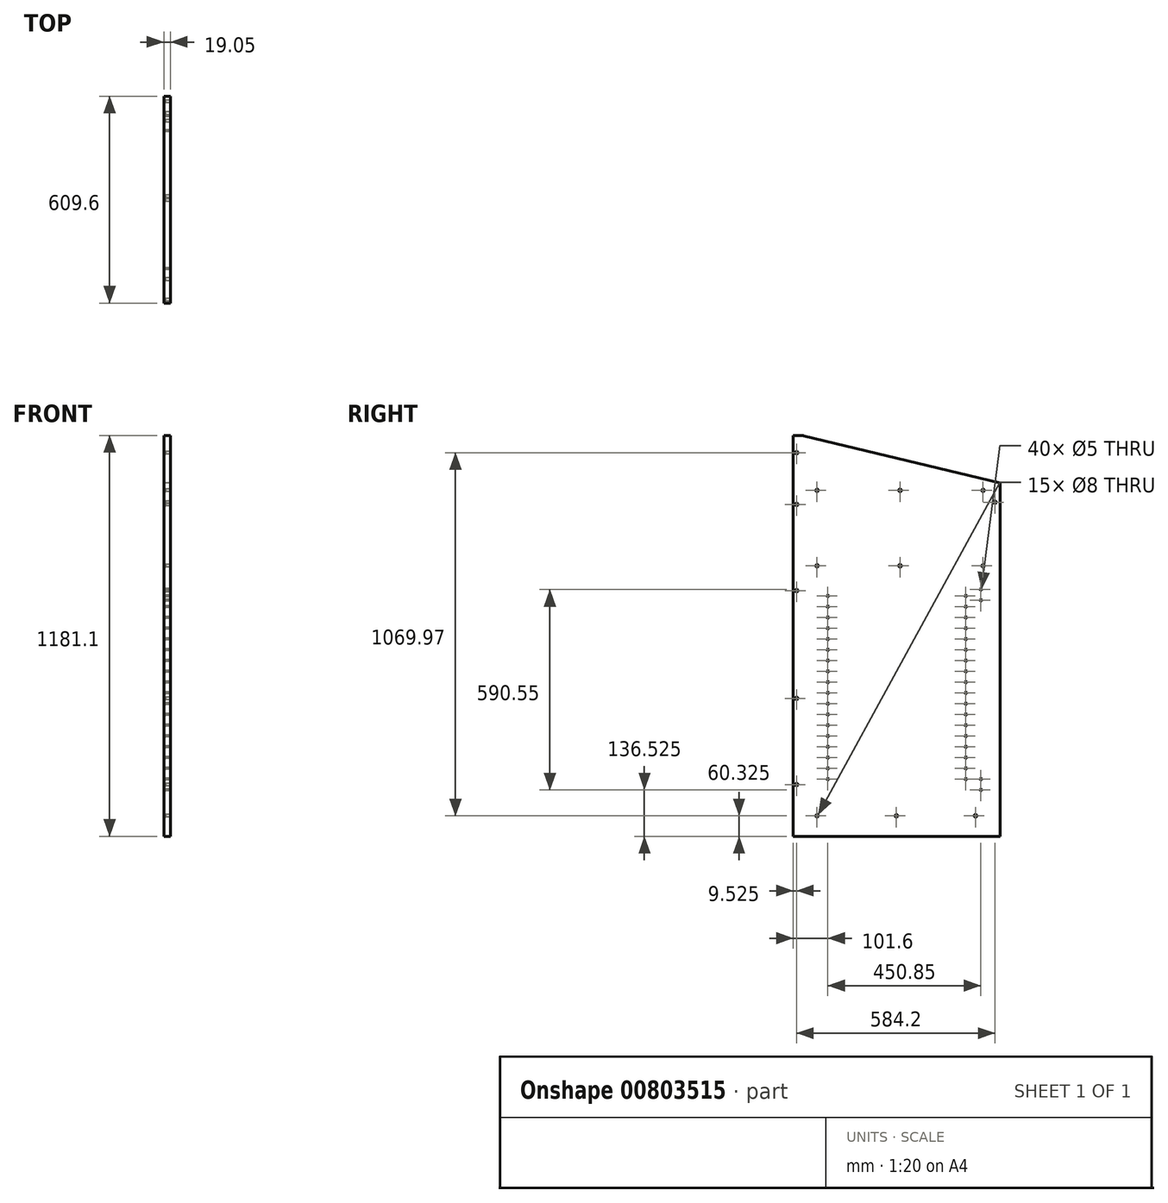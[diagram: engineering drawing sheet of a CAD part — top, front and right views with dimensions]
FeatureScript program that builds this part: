
annotation { "Feature Type Name" : "Feature", "Feature Type Description" : "" }
export const myFeature = defineFeature(function(context is Context, id is Id, definition is map)
    precondition{}
    {
        {
            var Q0;
            Q0=qCreatedBy(makeId("Right.planeOp"),FACE);
            var sketch = newSketch(context, id + "F0", { "sketchPlane" : qUnion([Q0])});
            skLineSegment(sketch, "E0.bottom", {"start": v(304.8, 590.55) * mm, "end": v(-304.8, 590.55) * mm});
            skLineSegment(sketch, "E0.top", {"start": v(304.8, -590.55) * mm, "end": v(-304.8, -590.55) * mm});
            skLineSegment(sketch, "E0.left", {"start": v(304.8, 590.55) * mm, "end": v(304.8, -590.55) * mm});
            skLineSegment(sketch, "E0.right", {"start": v(-304.8, 590.55) * mm, "end": v(-304.8, -590.55) * mm});
            skPoint(sketch, "E0.middle", {"position": v(0, 0) * mm});
            skLineSegment(sketch, "E1", {"start": v(304.8, 590.55) * mm, "end": v(285.39, 590.55) * mm});
            skLineSegment(sketch, "E2", {"start": v(-304.8, 590.55) * mm, "end": v(-304.8, 450.85) * mm});
            skLineSegment(sketch, "E3", {"start": v(-304.8, 450.85) * mm, "end": v(273.57, 589.16) * mm});
            skPoint(sketch, "E4.visualSharp", {"position": v(279.4, 590.55) * mm});
            skArc(sketch, "E4.filletArc", {"start": v(285.39, 590.55) * mm, "mid": v(279.44, 590.2) * mm, "end": v(273.57, 589.16) * mm});
            skLineSegment(sketch, "E5", {"start": v(-304.8, 450.85) * mm, "end": v(-304.8, 428.62) * mm});
            skSolve(sketch);
        }
        {
            var Q0;
            Q0=makeQuery(id+"F0.imprint","IMPRINT",FACE,{"disambiguationData":[TD([[makeQuery(id+"F0.imprint","IMPRINT",EDGE,{"derivedFrom":sQuery(id+"F0.wireOp",EDGE,"E0.top")}),-1.0]])]});
            extrude(context, id + "F1", {"entities" : qUnion([Q0]), "depth" : 19.05 * mm, "offsetDistance" : 25.4 * mm});
        }
        {
            var Q0;
            Q0=makeQuery(id+"F1.opExtrude","CAP_FACE",FACE,{"disambiguationData":[OSD([sQuery(id+"F0.wireOp",EDGE,"E0.top"),sQuery(id+"F0.wireOp",EDGE,"E0.left"),sQuery(id+"F0.wireOp",EDGE,"E0.right"),sQuery(id+"F0.wireOp",EDGE,"E1"),sQuery(id+"F0.wireOp",EDGE,"E3"),sQuery(id+"F0.wireOp",EDGE,"E4.filletArc"),sQuery(id+"F0.wireOp",EDGE,"E5")])],"isStart":false});
            var sketch = newSketch(context, id + "F2", { "sketchPlane" : qUnion([Q0])});
            skLineSegment(sketch, "E6.bottom", {"start": v(304.8, 590.55) * mm, "end": v(285.75, 590.55) * mm});
            skLineSegment(sketch, "E6.top", {"start": v(304.8, -590.55) * mm, "end": v(285.75, -590.55) * mm});
            skLineSegment(sketch, "E6.left", {"start": v(304.8, 590.55) * mm, "end": v(304.8, -590.55) * mm});
            skLineSegment(sketch, "E6.right", {"start": v(285.75, 590.55) * mm, "end": v(285.75, -590.55) * mm});
            skLineSegment(sketch, "E7", {"start": v(295.1, 590.55) * mm, "end": v(295.1, 539.75) * mm});
            skLineSegment(sketch, "E8", {"start": v(295.1, 590.55) * mm, "end": v(295.1, 387.35) * mm});
            skLineSegment(sketch, "E9", {"start": v(295.1, 590.55) * mm, "end": v(295.1, 133.35) * mm});
            skLineSegment(sketch, "E10", {"start": v(295.28, -590.55) * mm, "end": v(295.28, -438.15) * mm});
            skLineSegment(sketch, "E11", {"start": v(295.28, -590.55) * mm, "end": v(295.28, -184.15) * mm});
            skPoint(sketch, "E12", {"position": v(295.1, 539.75) * mm});
            skPoint(sketch, "E13", {"position": v(295.1, 387.35) * mm});
            skPoint(sketch, "E14", {"position": v(295.1, 133.35) * mm});
            skPoint(sketch, "E15", {"position": v(295.28, -184.15) * mm});
            skPoint(sketch, "E16", {"position": v(295.28, -438.15) * mm});
            skLineSegment(sketch, "E17", {"start": v(-304.8, 450.85) * mm, "end": v(-304.8, 438.15) * mm});
            skLineSegment(sketch, "E18.bottom", {"start": v(-304.8, 438.15) * mm, "end": v(285.75, 438.15) * mm});
            skLineSegment(sketch, "E18.top", {"start": v(-304.8, 419.1) * mm, "end": v(285.75, 419.1) * mm});
            skLineSegment(sketch, "E18.left", {"start": v(-304.8, 438.15) * mm, "end": v(-304.8, 419.1) * mm});
            skLineSegment(sketch, "E18.right", {"start": v(285.75, 438.15) * mm, "end": v(285.75, 419.1) * mm});
            skLineSegment(sketch, "E19", {"start": v(-304.8, -590.55) * mm, "end": v(-304.8, -539.75) * mm});
            skLineSegment(sketch, "E20", {"start": v(-304.8, -539.75) * mm, "end": v(-282.57, -539.75) * mm});
            skLineSegment(sketch, "E21.bottom", {"start": v(-282.57, -539.75) * mm, "end": v(285.75, -539.75) * mm});
            skLineSegment(sketch, "E21.top", {"start": v(-282.57, -511.18) * mm, "end": v(285.75, -511.18) * mm});
            skLineSegment(sketch, "E21.left", {"start": v(-282.57, -539.75) * mm, "end": v(-282.57, -511.18) * mm});
            skLineSegment(sketch, "E21.right", {"start": v(285.75, -539.75) * mm, "end": v(285.75, -511.18) * mm});
            skLineSegment(sketch, "E22", {"start": v(-304.8, 428.62) * mm, "end": v(-254, 428.62) * mm});
            skLineSegment(sketch, "E23", {"start": v(-9.52, 438.15) * mm, "end": v(-9.52, 428.62) * mm});
            skLineSegment(sketch, "E24", {"start": v(285.75, 428.62) * mm, "end": v(234.95, 428.62) * mm});
            skLineSegment(sketch, "E25", {"start": v(-304.8, 419.1) * mm, "end": v(-298.45, 419.1) * mm});
            skLineSegment(sketch, "E26.bottom", {"start": v(-298.45, 419.1) * mm, "end": v(-279.4, 419.1) * mm});
            skLineSegment(sketch, "E26.top", {"start": v(-298.45, 368.3) * mm, "end": v(-279.4, 368.3) * mm});
            skLineSegment(sketch, "E26.left", {"start": v(-298.45, 419.1) * mm, "end": v(-298.45, 368.3) * mm});
            skLineSegment(sketch, "E26.right", {"start": v(-279.4, 419.1) * mm, "end": v(-279.4, 368.3) * mm});
            skLineSegment(sketch, "E27", {"start": v(-288.92, 419.1) * mm, "end": v(-288.92, 393.7) * mm});
            skPoint(sketch, "E28", {"position": v(-288.92, 393.7) * mm});
            skPoint(sketch, "E29", {"position": v(-254, 428.62) * mm});
            skPoint(sketch, "E30", {"position": v(-9.52, 428.62) * mm});
            skPoint(sketch, "E31", {"position": v(234.95, 428.62) * mm});
            skLineSegment(sketch, "E32", {"start": v(-282.57, -539.75) * mm, "end": v(-282.57, -530.23) * mm});
            skLineSegment(sketch, "E33", {"start": v(-282.57, -530.23) * mm, "end": v(-231.77, -530.23) * mm});
            skLineSegment(sketch, "E34", {"start": v(-282.57, -530.23) * mm, "end": v(234.95, -530.23) * mm});
            skLineSegment(sketch, "E35", {"start": v(-282.57, -530.23) * mm, "end": v(-23.81, -530.23) * mm});
            skPoint(sketch, "E36", {"position": v(-231.77, -530.23) * mm});
            skPoint(sketch, "E37", {"position": v(234.95, -530.23) * mm});
            skLineSegment(sketch, "E38", {"start": v(-304.8, 419.1) * mm, "end": v(-304.8, 215.9) * mm});
            skLineSegment(sketch, "E39.bottom", {"start": v(-304.8, 215.9) * mm, "end": v(285.75, 215.9) * mm});
            skLineSegment(sketch, "E39.top", {"start": v(-304.8, 196.85) * mm, "end": v(285.75, 196.85) * mm});
            skLineSegment(sketch, "E39.left", {"start": v(-304.8, 215.9) * mm, "end": v(-304.8, 196.85) * mm});
            skLineSegment(sketch, "E39.right", {"start": v(285.75, 215.9) * mm, "end": v(285.75, 196.85) * mm});
            skLineSegment(sketch, "E40", {"start": v(-304.8, 206.37) * mm, "end": v(-254, 206.37) * mm});
            skLineSegment(sketch, "E41", {"start": v(285.75, 206.37) * mm, "end": v(234.95, 206.37) * mm});
            skLineSegment(sketch, "E42", {"start": v(-9.52, 215.9) * mm, "end": v(-9.52, 206.37) * mm});
            skPoint(sketch, "E43", {"position": v(-9.52, 206.37) * mm});
            skPoint(sketch, "E44", {"position": v(-254, 206.37) * mm});
            skPoint(sketch, "E45", {"position": v(234.95, 206.37) * mm});
            skLineSegment(sketch, "E46", {"start": v(-282.57, -530.23) * mm, "end": v(1.4, -530.23) * mm});
            skSolve(sketch);
        }
        {
            var Q0;
            Q0=sQuery(id+"F2.wireOp",VERTEX,"E29");
            var Q1;
            Q1=sQuery(id+"F2.wireOp",VERTEX,"E28");
            var Q2;
            Q2=sQuery(id+"F2.wireOp",VERTEX,"E30");
            var Q3;
            Q3=sQuery(id+"F2.wireOp",VERTEX,"E31");
            var Q4;
            Q4=sQuery(id+"F2.wireOp",VERTEX,"E44");
            var Q5;
            Q5=sQuery(id+"F2.wireOp",VERTEX,"E43");
            var Q6;
            Q6=sQuery(id+"F2.wireOp",VERTEX,"E45");
            var Q7;
            Q7=sQuery(id+"F2.wireOp",VERTEX,"E12");
            var Q8;
            Q8=sQuery(id+"F2.wireOp",VERTEX,"E13");
            var Q9;
            Q9=sQuery(id+"F2.wireOp",VERTEX,"E14");
            var Q10;
            Q10=sQuery(id+"F2.wireOp",VERTEX,"E15");
            var Q11;
            Q11=sQuery(id+"F2.wireOp",VERTEX,"E16");
            var Q12;
            Q12=sQuery(id+"F2.wireOp",VERTEX,"E37");
            var Q13;
            Q13=sQuery(id+"F2.wireOp",VERTEX,"E36");
            var Q14;
            Q14=sQuery(id+"F2.wireOp",VERTEX,"a019e4cf-f976-4d49-a43d-c813882953ad");
            var Q15;
            Q15=sQuery(id+"F2.wireOp",VERTEX,"E46.end");
            var Q16;
            Q16=makeQuery(id+"F1.opExtrude","SWEPT_BODY",BODY,{"disambiguationData":[OSD([sQuery(id+"F0.wireOp",EDGE,"E0.top"),sQuery(id+"F0.wireOp",EDGE,"E0.left"),sQuery(id+"F0.wireOp",EDGE,"E0.right"),sQuery(id+"F0.wireOp",EDGE,"E1"),sQuery(id+"F0.wireOp",EDGE,"E3"),sQuery(id+"F0.wireOp",EDGE,"E4.filletArc"),sQuery(id+"F0.wireOp",EDGE,"E5")])]});
            hole(context, id + "F3", {"style" : HoleStyle.SIMPLE, "endStyle" : HoleEndStyle.BLIND, "holeDiameter" : 8 * mm, "majorDiameter" : 6.35 * mm, "holeDepth" : 14.22 * mm, "isTappedThrough" : true, "tappedDepth" : 12.7 * mm, "tapClearance" : 3, "startFromSketch" : true, "locations" : qUnion([Q0, Q1, Q2, Q3, Q4, Q5, Q6, Q7, Q8, Q9, Q10, Q11, Q12, Q13, Q14, Q15]), "scope" : qUnion([Q16])});
        }
        {
            var Q0;
            Q0=makeQuery(id+"F1.opExtrude","CAP_FACE",FACE,{"disambiguationData":[OSD([sQuery(id+"F0.wireOp",EDGE,"E0.top"),sQuery(id+"F0.wireOp",EDGE,"E0.left"),sQuery(id+"F0.wireOp",EDGE,"E0.right"),sQuery(id+"F0.wireOp",EDGE,"E1"),sQuery(id+"F0.wireOp",EDGE,"E3"),sQuery(id+"F0.wireOp",EDGE,"E4.filletArc"),sQuery(id+"F0.wireOp",EDGE,"E5")])],"isStart":false});
            var sketch = newSketch(context, id + "F4", { "sketchPlane" : qUnion([Q0])});
            skLineSegment(sketch, "E47", {"start": v(0, -590.55) * mm, "end": v(0, -406.4) * mm});
            skLineSegment(sketch, "E48.bottom", {"start": v(203.2, -390.52) * mm, "end": v(-203.2, -390.52) * mm});
            skLineSegment(sketch, "E48.top", {"start": v(203.2, -422.27) * mm, "end": v(-203.2, -422.27) * mm});
            skLineSegment(sketch, "E48.left", {"start": v(203.2, -390.52) * mm, "end": v(203.2, -422.27) * mm});
            skLineSegment(sketch, "E48.right", {"start": v(-203.2, -390.52) * mm, "end": v(-203.2, -422.27) * mm});
            skPoint(sketch, "E48.middle", {"position": v(0, -406.4) * mm});
            skLineSegment(sketch, "E49.bottom", {"start": v(203.2, -358.77) * mm, "end": v(-203.2, -358.77) * mm});
            skLineSegment(sketch, "E49.top", {"start": v(203.2, -327.02) * mm, "end": v(-203.2, -327.02) * mm});
            skLineSegment(sketch, "E49.left", {"start": v(203.2, -358.77) * mm, "end": v(203.2, -327.02) * mm});
            skLineSegment(sketch, "E49.right", {"start": v(-203.2, -358.77) * mm, "end": v(-203.2, -327.02) * mm});
            skPoint(sketch, "E49.middle", {"position": v(0, -342.9) * mm});
            skLineSegment(sketch, "E50", {"start": v(0, -342.9) * mm, "end": v(0, -279.4) * mm});
            skLineSegment(sketch, "E51.bottom", {"start": v(203.2, -295.27) * mm, "end": v(-203.2, -295.27) * mm});
            skLineSegment(sketch, "E51.top", {"start": v(203.2, -263.52) * mm, "end": v(-203.2, -263.52) * mm});
            skLineSegment(sketch, "E51.left", {"start": v(203.2, -295.27) * mm, "end": v(203.2, -263.52) * mm});
            skLineSegment(sketch, "E51.right", {"start": v(-203.2, -295.27) * mm, "end": v(-203.2, -263.52) * mm});
            skPoint(sketch, "E51.middle", {"position": v(0, -279.4) * mm});
            skLineSegment(sketch, "E52", {"start": v(0, -279.4) * mm, "end": v(0, -215.9) * mm});
            skLineSegment(sketch, "E53.bottom", {"start": v(-203.2, -231.77) * mm, "end": v(203.2, -231.77) * mm});
            skLineSegment(sketch, "E53.top", {"start": v(-203.2, -200.02) * mm, "end": v(203.2, -200.02) * mm});
            skLineSegment(sketch, "E53.left", {"start": v(-203.2, -231.77) * mm, "end": v(-203.2, -200.02) * mm});
            skLineSegment(sketch, "E53.right", {"start": v(203.2, -231.77) * mm, "end": v(203.2, -200.02) * mm});
            skPoint(sketch, "E53.middle", {"position": v(0, -215.9) * mm});
            skLineSegment(sketch, "E54", {"start": v(0, -215.9) * mm, "end": v(0, -152.4) * mm});
            skLineSegment(sketch, "E55.bottom", {"start": v(-203.2, -168.27) * mm, "end": v(203.2, -168.27) * mm});
            skLineSegment(sketch, "E55.top", {"start": v(-203.2, -136.52) * mm, "end": v(203.2, -136.52) * mm});
            skLineSegment(sketch, "E55.left", {"start": v(-203.2, -168.27) * mm, "end": v(-203.2, -136.52) * mm});
            skLineSegment(sketch, "E55.right", {"start": v(203.2, -168.27) * mm, "end": v(203.2, -136.52) * mm});
            skPoint(sketch, "E55.middle", {"position": v(0, -152.4) * mm});
            skLineSegment(sketch, "E56", {"start": v(0, -152.4) * mm, "end": v(0, -88.9) * mm});
            skLineSegment(sketch, "E57.bottom", {"start": v(-203.2, -104.77) * mm, "end": v(203.2, -104.77) * mm});
            skLineSegment(sketch, "E57.top", {"start": v(-203.2, -73.02) * mm, "end": v(203.2, -73.02) * mm});
            skLineSegment(sketch, "E57.left", {"start": v(-203.2, -104.77) * mm, "end": v(-203.2, -73.02) * mm});
            skLineSegment(sketch, "E57.right", {"start": v(203.2, -104.77) * mm, "end": v(203.2, -73.02) * mm});
            skPoint(sketch, "E57.middle", {"position": v(0, -88.9) * mm});
            skLineSegment(sketch, "E58", {"start": v(0, -88.9) * mm, "end": v(0, -25.4) * mm});
            skLineSegment(sketch, "E59.bottom", {"start": v(-203.2, -41.27) * mm, "end": v(203.2, -41.27) * mm});
            skLineSegment(sketch, "E59.top", {"start": v(-203.2, -9.52) * mm, "end": v(203.2, -9.52) * mm});
            skLineSegment(sketch, "E59.left", {"start": v(-203.2, -41.27) * mm, "end": v(-203.2, -9.52) * mm});
            skLineSegment(sketch, "E59.right", {"start": v(203.2, -41.27) * mm, "end": v(203.2, -9.52) * mm});
            skPoint(sketch, "E59.middle", {"position": v(0, -25.4) * mm});
            skLineSegment(sketch, "E60", {"start": v(0, -25.4) * mm, "end": v(0, 38.1) * mm});
            skLineSegment(sketch, "E61.bottom", {"start": v(-203.2, 53.98) * mm, "end": v(203.2, 53.98) * mm});
            skLineSegment(sketch, "E61.top", {"start": v(-203.2, 22.23) * mm, "end": v(203.2, 22.23) * mm});
            skLineSegment(sketch, "E61.left", {"start": v(-203.2, 53.98) * mm, "end": v(-203.2, 22.23) * mm});
            skLineSegment(sketch, "E61.right", {"start": v(203.2, 53.98) * mm, "end": v(203.2, 22.23) * mm});
            skPoint(sketch, "E61.middle", {"position": v(0, 38.1) * mm});
            skLineSegment(sketch, "E62", {"start": v(0, 38.1) * mm, "end": v(0, 101.6) * mm});
            skLineSegment(sketch, "E63.bottom", {"start": v(-203.2, 85.73) * mm, "end": v(203.2, 85.73) * mm});
            skLineSegment(sketch, "E63.top", {"start": v(-203.2, 117.48) * mm, "end": v(203.2, 117.48) * mm});
            skLineSegment(sketch, "E63.left", {"start": v(-203.2, 85.73) * mm, "end": v(-203.2, 117.48) * mm});
            skLineSegment(sketch, "E63.right", {"start": v(203.2, 85.73) * mm, "end": v(203.2, 117.48) * mm});
            skPoint(sketch, "E63.middle", {"position": v(0, 101.6) * mm});
            skSolve(sketch);
        }
        {
            var Q0;
            Q0=sQuery(id+"F4.wireOp",VERTEX,"E63.top.start");
            var Q1;
            Q1=sQuery(id+"F4.wireOp",VERTEX,"E63.bottom.start");
            var Q2;
            Q2=sQuery(id+"F4.wireOp",VERTEX,"E61.bottom.start");
            var Q3;
            Q3=sQuery(id+"F4.wireOp",VERTEX,"E61.top.start");
            var Q4;
            Q4=sQuery(id+"F4.wireOp",VERTEX,"E59.top.start");
            var Q5;
            Q5=sQuery(id+"F4.wireOp",VERTEX,"E59.bottom.start");
            var Q6;
            Q6=sQuery(id+"F4.wireOp",VERTEX,"E57.top.start");
            var Q7;
            Q7=sQuery(id+"F4.wireOp",VERTEX,"E57.bottom.start");
            var Q8;
            Q8=sQuery(id+"F4.wireOp",VERTEX,"E55.top.start");
            var Q9;
            Q9=sQuery(id+"F4.wireOp",VERTEX,"E55.bottom.start");
            var Q10;
            Q10=sQuery(id+"F4.wireOp",VERTEX,"E53.top.start");
            var Q11;
            Q11=sQuery(id+"F4.wireOp",VERTEX,"E53.bottom.start");
            var Q12;
            Q12=sQuery(id+"F4.wireOp",VERTEX,"E51.top.end");
            var Q13;
            Q13=sQuery(id+"F4.wireOp",VERTEX,"E51.bottom.end");
            var Q14;
            Q14=sQuery(id+"F4.wireOp",VERTEX,"E49.top.end");
            var Q15;
            Q15=sQuery(id+"F4.wireOp",VERTEX,"E49.bottom.end");
            var Q16;
            Q16=sQuery(id+"F4.wireOp",VERTEX,"E48.bottom.end");
            var Q17;
            Q17=sQuery(id+"F4.wireOp",VERTEX,"E48.top.end");
            var Q18;
            Q18=sQuery(id+"F4.wireOp",VERTEX,"E48.top.start");
            var Q19;
            Q19=sQuery(id+"F4.wireOp",VERTEX,"E48.bottom.start");
            var Q20;
            Q20=sQuery(id+"F4.wireOp",VERTEX,"E49.bottom.start");
            var Q21;
            Q21=sQuery(id+"F4.wireOp",VERTEX,"E49.top.start");
            var Q22;
            Q22=sQuery(id+"F4.wireOp",VERTEX,"E51.bottom.start");
            var Q23;
            Q23=sQuery(id+"F4.wireOp",VERTEX,"E51.top.start");
            var Q24;
            Q24=sQuery(id+"F4.wireOp",VERTEX,"E53.bottom.end");
            var Q25;
            Q25=sQuery(id+"F4.wireOp",VERTEX,"E53.top.end");
            var Q26;
            Q26=sQuery(id+"F4.wireOp",VERTEX,"E55.bottom.end");
            var Q27;
            Q27=sQuery(id+"F4.wireOp",VERTEX,"E55.top.end");
            var Q28;
            Q28=sQuery(id+"F4.wireOp",VERTEX,"E57.bottom.end");
            var Q29;
            Q29=sQuery(id+"F4.wireOp",VERTEX,"E57.top.end");
            var Q30;
            Q30=sQuery(id+"F4.wireOp",VERTEX,"E59.bottom.end");
            var Q31;
            Q31=sQuery(id+"F4.wireOp",VERTEX,"E59.top.end");
            var Q32;
            Q32=sQuery(id+"F4.wireOp",VERTEX,"E61.top.end");
            var Q33;
            Q33=sQuery(id+"F4.wireOp",VERTEX,"E61.bottom.end");
            var Q34;
            Q34=sQuery(id+"F4.wireOp",VERTEX,"E63.bottom.end");
            var Q35;
            Q35=sQuery(id+"F4.wireOp",VERTEX,"E63.top.end");
            var Q36;
            Q36=makeQuery(id+"F1.opExtrude","SWEPT_BODY",BODY,{"disambiguationData":[OSD([sQuery(id+"F0.wireOp",EDGE,"E0.top"),sQuery(id+"F0.wireOp",EDGE,"E0.left"),sQuery(id+"F0.wireOp",EDGE,"E0.right"),sQuery(id+"F0.wireOp",EDGE,"E1"),sQuery(id+"F0.wireOp",EDGE,"E3"),sQuery(id+"F0.wireOp",EDGE,"E4.filletArc"),sQuery(id+"F0.wireOp",EDGE,"E5")])]});
            hole(context, id + "F5", {"style" : HoleStyle.SIMPLE, "endStyle" : HoleEndStyle.BLIND, "holeDiameter" : 5 * mm, "majorDiameter" : 6.35 * mm, "holeDepth" : 14.22 * mm, "isTappedThrough" : true, "tappedDepth" : 12.7 * mm, "tapClearance" : 3, "startFromSketch" : true, "locations" : qUnion([Q0, Q1, Q2, Q3, Q4, Q5, Q6, Q7, Q8, Q9, Q10, Q11, Q12, Q13, Q14, Q15, Q16, Q17, Q18, Q19, Q20, Q21, Q22, Q23, Q24, Q25, Q26, Q27, Q28, Q29, Q30, Q31, Q32, Q33, Q34, Q35]), "scope" : qUnion([Q36])});
        }
        {
            var Q0;
            Q0=makeQuery(id+"F1.opExtrude","SWEPT_BODY",BODY,{"disambiguationData":[OSD([sQuery(id+"F0.wireOp",EDGE,"E0.top"),sQuery(id+"F0.wireOp",EDGE,"E0.left"),sQuery(id+"F0.wireOp",EDGE,"E0.right"),sQuery(id+"F0.wireOp",EDGE,"E1"),sQuery(id+"F0.wireOp",EDGE,"E3"),sQuery(id+"F0.wireOp",EDGE,"E4.filletArc"),sQuery(id+"F0.wireOp",EDGE,"E5")])]});
            var Q1;
            Q1=makeQuery(id+"F1.opExtrude","SWEPT_FACE",FACE,{"disambiguationData":[OSD([sQuery(id+"F0.wireOp",EDGE,"E0.left")])]});
            mirror(context, id + "F6", {"entities" : qUnion([Q0]), "mirrorPlane" : qUnion([Q1])});
        }
        {
            var Q0;
            Q0=makeQuery(id+"F1.opExtrude","SWEPT_BODY",BODY,{"disambiguationData":[OSD([sQuery(id+"F0.wireOp",EDGE,"E0.top"),sQuery(id+"F0.wireOp",EDGE,"E0.left"),sQuery(id+"F0.wireOp",EDGE,"E0.right"),sQuery(id+"F0.wireOp",EDGE,"E1"),sQuery(id+"F0.wireOp",EDGE,"E3"),sQuery(id+"F0.wireOp",EDGE,"E4.filletArc"),sQuery(id+"F0.wireOp",EDGE,"E5")])]});
            deleteBodies(context, id + "F7", {"entities" : qUnion([Q0])});
        }
        {
            var Q0;
            Q0=makeQuery(id+"F6.opPattern","COPY",FACE,{"derivedFrom":makeQuery(id+"F1.opExtrude","CAP_FACE",FACE,{"disambiguationData":[OSD([sQuery(id+"F0.wireOp",EDGE,"E0.top"),sQuery(id+"F0.wireOp",EDGE,"E0.left"),sQuery(id+"F0.wireOp",EDGE,"E0.right"),sQuery(id+"F0.wireOp",EDGE,"E1"),sQuery(id+"F0.wireOp",EDGE,"E3"),sQuery(id+"F0.wireOp",EDGE,"E4.filletArc"),sQuery(id+"F0.wireOp",EDGE,"E5")])],"isStart":false}),"instanceName":"1"});
            var sketch = newSketch(context, id + "F8", { "sketchPlane" : qUnion([Q0])});
            skLineSegment(sketch, "E64.bottom", {"start": v(914.4, 215.9) * mm, "end": v(323.85, 215.9) * mm});
            skLineSegment(sketch, "E64.top", {"start": v(914.4, 196.85) * mm, "end": v(323.85, 196.85) * mm});
            skLineSegment(sketch, "E64.left", {"start": v(914.4, 215.9) * mm, "end": v(914.4, 196.85) * mm});
            skLineSegment(sketch, "E64.right", {"start": v(323.85, 215.9) * mm, "end": v(323.85, 196.85) * mm});
            skPoint(sketch, "E64.middle", {"position": v(619.13, 206.37) * mm});
            skLineSegment(sketch, "E65", {"start": v(914.4, 196.85) * mm, "end": v(914.4, 120.65) * mm});
            skLineSegment(sketch, "E66", {"start": v(914.4, 120.65) * mm, "end": v(857.25, 120.65) * mm});
            skLineSegment(sketch, "E67", {"start": v(857.25, 120.65) * mm, "end": v(857.25, 136.53) * mm});
            skLineSegment(sketch, "E68", {"start": v(857.25, 120.65) * mm, "end": v(857.25, 104.78) * mm});
            skPoint(sketch, "E69", {"position": v(857.25, 136.53) * mm});
            skPoint(sketch, "E70", {"position": v(857.25, 104.78) * mm});
            skLineSegment(sketch, "E71", {"start": v(914.4, -590.55) * mm, "end": v(914.4, -438.15) * mm});
            skLineSegment(sketch, "E72", {"start": v(914.4, -438.15) * mm, "end": v(857.25, -438.15) * mm});
            skLineSegment(sketch, "E73", {"start": v(857.25, -438.15) * mm, "end": v(857.25, -422.28) * mm});
            skLineSegment(sketch, "E74", {"start": v(857.25, -438.15) * mm, "end": v(857.25, -454.03) * mm});
            skPoint(sketch, "E75", {"position": v(857.25, -422.28) * mm});
            skPoint(sketch, "E76", {"position": v(857.25, -454.03) * mm});
            skSolve(sketch);
        }
        {
            var Q0;
            Q0=sQuery(id+"F8.wireOp",VERTEX,"E69");
            var Q1;
            Q1=sQuery(id+"F8.wireOp",VERTEX,"E70");
            var Q2;
            Q2=sQuery(id+"F8.wireOp",VERTEX,"E73.end");
            var Q3;
            Q3=sQuery(id+"F8.wireOp",VERTEX,"E76");
            var Q4;
            Q4=makeQuery(id+"F6.opPattern","COPY",BODY,{"derivedFrom":makeQuery(id+"F1.opExtrude","SWEPT_BODY",BODY,{"disambiguationData":[OSD([sQuery(id+"F0.wireOp",EDGE,"E0.top"),sQuery(id+"F0.wireOp",EDGE,"E0.left"),sQuery(id+"F0.wireOp",EDGE,"E0.right"),sQuery(id+"F0.wireOp",EDGE,"E1"),sQuery(id+"F0.wireOp",EDGE,"E3"),sQuery(id+"F0.wireOp",EDGE,"E4.filletArc"),sQuery(id+"F0.wireOp",EDGE,"E5")])]}),"instanceName":"1"});
            hole(context, id + "F9", {"style" : HoleStyle.SIMPLE, "endStyle" : HoleEndStyle.BLIND, "holeDiameter" : 5 * mm, "majorDiameter" : 6.35 * mm, "holeDepth" : 14.22 * mm, "isTappedThrough" : true, "tappedDepth" : 12.7 * mm, "tapClearance" : 3, "startFromSketch" : true, "locations" : qUnion([Q0, Q1, Q2, Q3]), "scope" : qUnion([Q4])});
        }
    });
